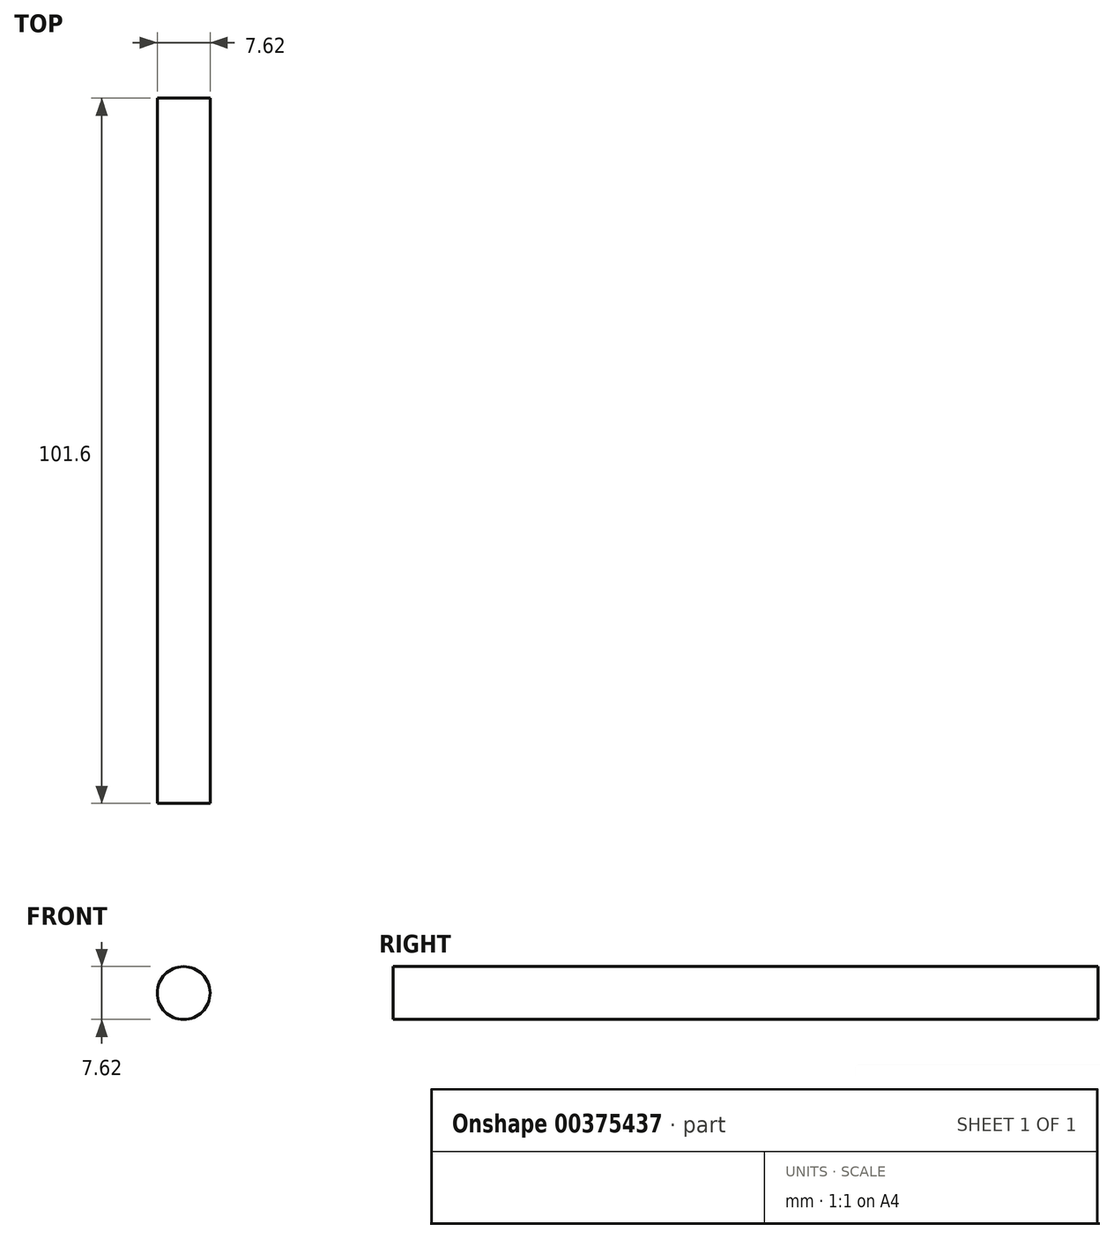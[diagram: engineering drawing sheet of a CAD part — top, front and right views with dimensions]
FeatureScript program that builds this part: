
annotation { "Feature Type Name" : "Feature", "Feature Type Description" : "" }
export const myFeature = defineFeature(function(context is Context, id is Id, definition is map)
    precondition{}
    {
        {
            var Q0;
            Q0=qCreatedBy(makeId("Front.planeOp"),FACE);
            var sketch = newSketch(context, id + "F0", { "sketchPlane" : qUnion([Q0])});
            skCircle(sketch, "E0", {"center": v(0, 0) * mm, "radius": 3.81 * mm});
            skSolve(sketch);
        }
        {
            var Q0;
            Q0 = qSketchRegion(id + "F0", true);
            extrude(context, id + "F1", {"entities" : qUnion([Q0]), "depth" : 101.6 * mm});
        }
    });
